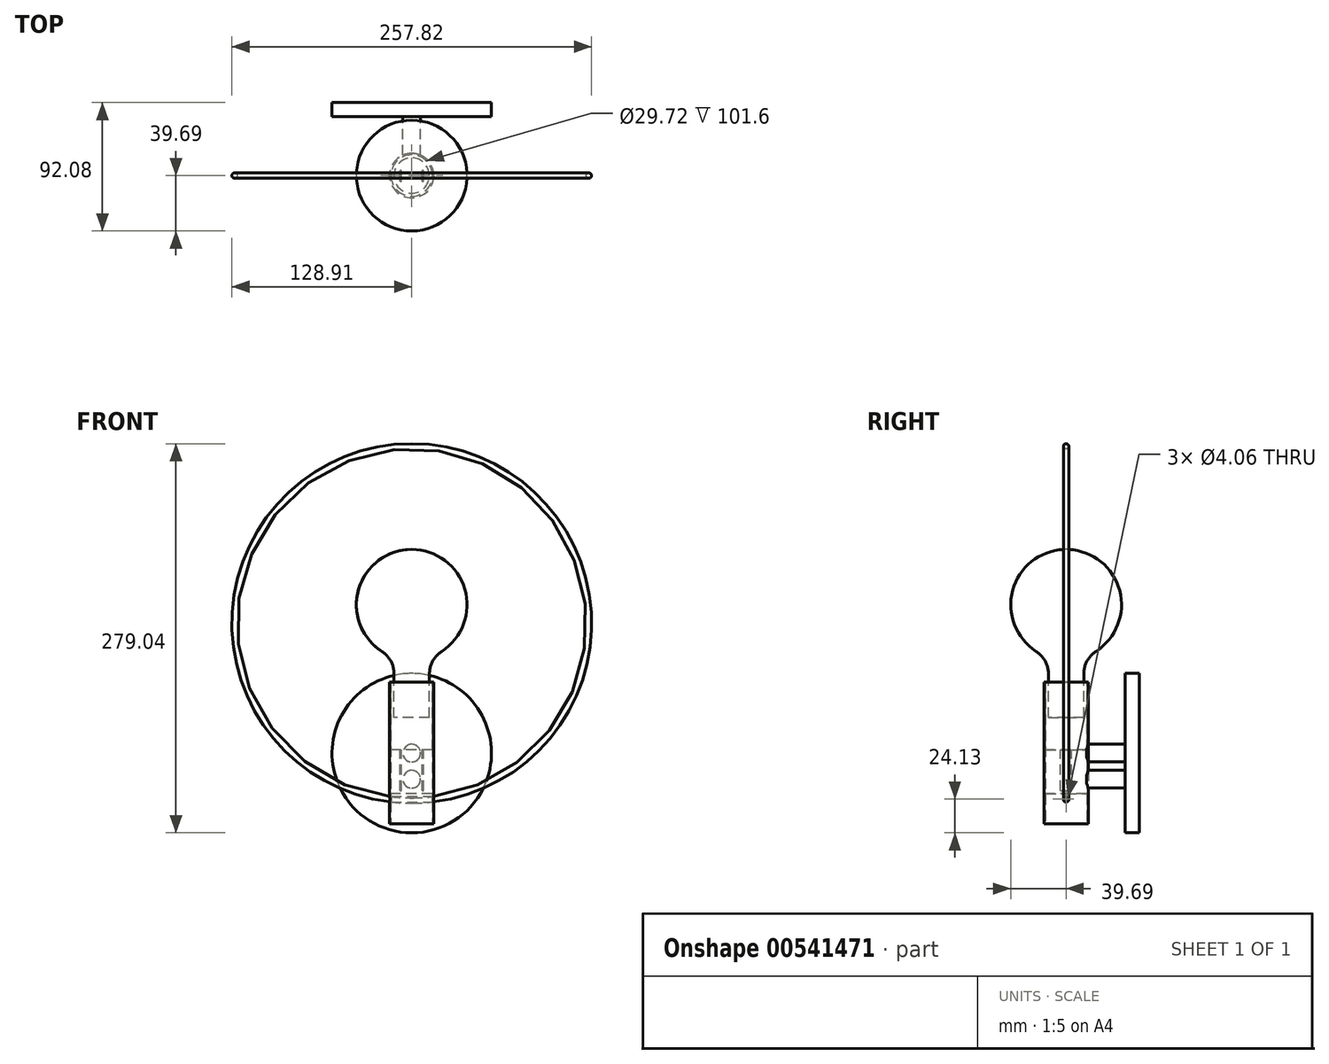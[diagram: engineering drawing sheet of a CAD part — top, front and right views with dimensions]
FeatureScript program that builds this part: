
annotation { "Feature Type Name" : "Feature", "Feature Type Description" : "" }
export const myFeature = defineFeature(function(context is Context, id is Id, definition is map)
    precondition{}
    {
        {
            var Q0;
            Q0=qCreatedBy(makeId("Top.planeOp"),FACE);
            var sketch = newSketch(context, id + "F0", { "sketchPlane" : qUnion([Q0])});
            skCircle(sketch, "E0", {"center": v(0, 0) * mm, "radius": 15.88 * mm});
            skCircle(sketch, "E1", {"center": v(0, 0) * mm, "radius": 14.86 * mm});
            skSolve(sketch);
        }
        {
            var Q0;
            Q0=makeQuery(id+"F0.imprint","IMPRINT",FACE,{"disambiguationData":[TD([[makeQuery(id+"F0.imprint","IMPRINT",EDGE,{"derivedFrom":sQuery(id+"F0.wireOp",EDGE,"E1")}),-1.0]])]});
            extrude(context, id + "F1", {"entities" : qUnion([Q0]), "depth" : 101.6 * mm, "offsetDistance" : 25.4 * mm});
        }
        {
            var Q0;
            Q0=makeQuery(id+"F0.imprint","IMPRINT",FACE,{"disambiguationData":[TD([[makeQuery(id+"F0.imprint","IMPRINT",EDGE,{"derivedFrom":sQuery(id+"F0.wireOp",EDGE,"E1")}),1.0]])]});
            var Q1;
            Q1=sQuery(id+"F0.wireOp",EDGE,"E1");
            extrude(context, id + "F2", {"entities" : qUnion([Q0]), "surfaceEntities" : qUnion([Q1]), "depth" : 21.59 * mm, "offsetDistance" : 25.4 * mm});
        }
        {
            var Q0;
            Q0=qCreatedBy(makeId("Front.planeOp"),FACE);
            var sketch = newSketch(context, id + "F3", { "sketchPlane" : qUnion([Q0])});
            skArc(sketch, "E2", {"start": v(21.45, 123.77) * mm, "mid": v(0, 196.85) * mm, "end": v(-21.45, 123.77) * mm});
            skLineSegment(sketch, "E3.top", {"start": v(-12.7, 76.2) * mm, "end": v(12.7, 76.2) * mm});
            skLineSegment(sketch, "E3.left", {"start": v(-12.7, 107.75) * mm, "end": v(-12.7, 76.2) * mm});
            skLineSegment(sketch, "E3.right", {"start": v(12.7, 107.75) * mm, "end": v(12.7, 76.2) * mm});
            skPoint(sketch, "E4.visualSharp", {"position": v(-12.7, 119.56) * mm});
            skArc(sketch, "E4.filletArc", {"start": v(-12.7, 107.75) * mm, "mid": v(-15.03, 116.88) * mm, "end": v(-21.45, 123.77) * mm});
            skPoint(sketch, "E5.visualSharp", {"position": v(12.7, 119.56) * mm});
            skArc(sketch, "E5.filletArc", {"start": v(21.45, 123.77) * mm, "mid": v(15.03, 116.88) * mm, "end": v(12.7, 107.75) * mm});
            skLineSegment(sketch, "E6", {"start": v(0, 196.85) * mm, "end": v(0, 76.2) * mm});
            skSolve(sketch);
        }
        {
            var Q0;
            {var subQ0=sQuery(id+"F3.wireOp",EDGE,"E3.left");Q0=makeQuery(id+"F3.imprint","IMPRINT",FACE,{"disambiguationData":[TD([[makeQuery(id+"F3.imprint","IMPRINT",EDGE,{"derivedFrom":subQ0}),1.0]])]});}
            var Q1;
            Q1=sQuery(id+"F3.wireOp",EDGE,"E6");
            revolve(context, id + "F4", {"entities" : qUnion([Q0]), "axis" : qUnion([Q1]), "revolveType" : RevolveType.FULL});
        }
        {
            var Q0;
            Q0=qCreatedBy(makeId("Right.planeOp"),FACE);
            var sketch = newSketch(context, id + "F5", { "sketchPlane" : qUnion([Q0])});
            skCircle(sketch, "E7", {"center": v(0, 17.78) * mm, "radius": 2.03 * mm});
            skSolve(sketch);
        }
        {
            var Q0;
            Q0=qSketchRegion(id+"F5",true);
            extrude(context, id + "F6", {"entities" : qUnion([Q0]), "operationType" : NewBodyOperationType.REMOVE, "endBound" : BoundingType.THROUGH_ALL, "oppositeDirection" : true, "depth" : 25.4 * mm, "offsetDistance" : 25.4 * mm, "hasSecondDirection" : true, "secondDirectionBound" : BoundingType.THROUGH_ALL, "secondDirectionOppositeDirection" : false, "secondDirectionDepth" : 25.4 * mm});
        }
        {
            var Q0;
            Q0=qCreatedBy(makeId("Front.planeOp"),FACE);
            var sketch = newSketch(context, id + "F7", { "sketchPlane" : qUnion([Q0])});
            skCircle(sketch, "E8", {"center": v(0, 143.78) * mm, "radius": 127 * mm});
            skFitSpline(sketch, "E9.0", {"points": [v(-15.88, 19.81) * mm, v(-15.88, 19.81) * mm, v(-15.86, 19.7) * mm, v(-15.8, 19.25) * mm, v(-15.77, 18.7) * mm, v(-15.75, 18.18) * mm, v(-15.74, 17.78) * mm, v(-15.75, 17.38) * mm, v(-15.76, 17) * mm, v(-15.78, 16.64) * mm, v(-15.82, 16.23) * mm, v(-15.86, 15.85) * mm, v(-15.88, 15.75) * mm, v(-15.87, 15.75) * mm], "construction": true});
            skLineSegment(sketch, "E10", {"start": v(-15.88, 19.81) * mm, "end": v(-15.87, 15.75) * mm, "construction": true});
            skPoint(sketch, "E11", {"position": v(-15.87, 17.78) * mm});
            skSolve(sketch);
        }
        {
            var Q0;
            Q0=qCreatedBy(makeId("Right.planeOp"),FACE);
            var sketch = newSketch(context, id + "F8", { "sketchPlane" : qUnion([Q0])});
            skCircle(sketch, "E12", {"center": v(0, 16.78) * mm, "radius": 1.9 * mm});
            skSolve(sketch);
        }
        {
            var Q0;
            Q0=qSketchRegion(id+"F8",true);
            var Q1;
            Q1=qConstructionFilter(qBodyType(qCreatedBy(id+"F7",EDGE),BodyType.WIRE),ConstructionObject.NO);
            sweep(context, id + "F9", {"profiles" : qUnion([Q0]), "path" : qUnion([Q1])});
        }
        {
            var Q0;
            Q0=qCreatedBy(makeId("Right.planeOp"),FACE);
            var sketch = newSketch(context, id + "F10", { "sketchPlane" : qUnion([Q0])});
            skArc(sketch, "E13", {"start": v(21.45, 123.77) * mm, "mid": v(0, 196.85) * mm, "end": v(-21.45, 123.77) * mm});
            skLineSegment(sketch, "E14", {"start": v(39.69, 157.16) * mm, "end": v(39.69, 209.78) * mm});
            skSolve(sketch);
        }
        {
            var Q0;
            Q0=qCreatedBy(makeId("Front.planeOp"),FACE);
            var Q1;
            Q1=sQuery(id+"F10.wireOp",VERTEX,"E14.end");
            cPlane(context, id + "F11", {"entities" : qUnion([Q0, Q1]), "cplaneType" : CPlaneType.PLANE_POINT, "offset" : 25.4 * mm, "width" : 152.4 * mm, "height" : 152.4 * mm});
        }
        {
            var Q0;
            Q0=qCreatedBy(id+"F11.planeOp",FACE);
            cPlane(context, id + "F12", {"entities" : qUnion([Q0]), "cplaneType" : CPlaneType.OFFSET, "offset" : 2.54 * mm, "oppositeDirection" : true, "width" : 152.4 * mm, "height" : 152.4 * mm});
        }
        {
            var Q0;
            Q0=qCreatedBy(id+"F12.planeOp",FACE);
            var sketch = newSketch(context, id + "F13", { "sketchPlane" : qUnion([Q0])});
            skCircle(sketch, "E15", {"center": v(0, 50.8) * mm, "radius": 57.15 * mm});
            skLineSegment(sketch, "E16.0", {"start": v(-15.88, 101.6) * mm, "end": v(15.88, 101.6) * mm, "construction": true});
            skLineSegment(sketch, "E17.0", {"start": v(-15.88, 0) * mm, "end": v(15.88, 0) * mm, "construction": true});
            skLineSegment(sketch, "E18", {"start": v(0, 101.6) * mm, "end": v(0, 0) * mm, "construction": true});
            skCircle(sketch, "E19", {"center": v(0, 50.8) * mm, "radius": 6.35 * mm});
            skCircle(sketch, "E20", {"center": v(0, 32.06) * mm, "radius": 6.35 * mm});
            skSolve(sketch);
        }
        {
            var Q0;
            Q0=makeQuery(id+"F13.imprint","IMPRINT",FACE,{"disambiguationData":[TD([[makeQuery(id+"F13.imprint","IMPRINT",EDGE,{"derivedFrom":sQuery(id+"F13.wireOp",EDGE,"E19")}),1.0]])]});
            var Q1;
            Q1=makeQuery(id+"F13.imprint","IMPRINT",FACE,{"disambiguationData":[TD([[makeQuery(id+"F13.imprint","IMPRINT",EDGE,{"derivedFrom":sQuery(id+"F13.wireOp",EDGE,"E20")}),1.0]])]});
            var Q2;
            Q2=makeQuery(id+"F1.opExtrude","SWEPT_FACE",FACE,{"disambiguationData":[OSD([sQuery(id+"F0.wireOp",EDGE,"E0")])]});
            extrude(context, id + "F14", {"entities" : qUnion([Q0, Q1]), "endBound" : BoundingType.UP_TO_SURFACE, "depth" : 25.4 * mm, "endBoundEntityFace" : qUnion([Q2]), "offsetDistance" : 25.4 * mm});
        }
        {
            var Q0;
            Q0=makeQuery(id+"F13.imprint","IMPRINT",FACE,{"disambiguationData":[TD([[makeQuery(id+"F13.imprint","IMPRINT",EDGE,{"derivedFrom":sQuery(id+"F13.wireOp",EDGE,"E15")}),1.0]])]});
            var Q1;
            Q1=makeQuery(id+"F13.imprint","IMPRINT",FACE,{"disambiguationData":[TD([[makeQuery(id+"F13.imprint","IMPRINT",EDGE,{"derivedFrom":sQuery(id+"F13.wireOp",EDGE,"E20")}),1.0]])]});
            var Q2;
            Q2=makeQuery(id+"F13.imprint","IMPRINT",FACE,{"disambiguationData":[TD([[makeQuery(id+"F13.imprint","IMPRINT",EDGE,{"derivedFrom":sQuery(id+"F13.wireOp",EDGE,"E19")}),1.0]])]});
            extrude(context, id + "F15", {"entities" : qUnion([Q0, Q1, Q2]), "oppositeDirection" : true, "depth" : 10.16 * mm, "offsetDistance" : 25.4 * mm});
        }
        {
            var Q0;
            Q0=makeQuery(id+"F1.opExtrude","CAP_FACE",FACE,{"disambiguationData":[OSD([sQuery(id+"F0.wireOp",EDGE,"E0"),sQuery(id+"F0.wireOp",EDGE,"E1")])],"isStart":false});
            var sketch = newSketch(context, id + "F16", { "sketchPlane" : qUnion([Q0])});
            skCircle(sketch, "E21.0", {"center": v(0, 0) * mm, "radius": 14.86 * mm});
            skSolve(sketch);
        }
        {
            var Q0;
            Q0 = qSketchRegion(id + "F16", true);
            extrude(context, id + "F17", {"entities" : qUnion([Q0]), "oppositeDirection" : true, "depth" : 48.58 * mm, "offsetDistance" : 25.4 * mm});
        }
        {
            var Q0;
            Q0=makeQuery(id+"F17.opExtrude","CAP_FACE",FACE,{"disambiguationData":[OSD([sQuery(id+"F16.wireOp",EDGE,"E21.0")])],"isStart":false});
            var sketch = newSketch(context, id + "F18", { "sketchPlane" : qUnion([Q0])});
            skLineSegment(sketch, "E22.bottom", {"start": v(7.43, 3.97) * mm, "end": v(8.45, 3.97) * mm});
            skLineSegment(sketch, "E22.top", {"start": v(7.43, -3.97) * mm, "end": v(8.45, -3.97) * mm});
            skLineSegment(sketch, "E22.left", {"start": v(7.43, 3.97) * mm, "end": v(7.43, -3.97) * mm});
            skLineSegment(sketch, "E22.right", {"start": v(8.45, 3.97) * mm, "end": v(8.45, -3.97) * mm});
            skLineSegment(sketch, "E23.bottom", {"start": v(-8.45, 3.97) * mm, "end": v(-7.43, 3.97) * mm});
            skLineSegment(sketch, "E23.top", {"start": v(-8.45, -3.97) * mm, "end": v(-7.43, -3.97) * mm});
            skLineSegment(sketch, "E23.left", {"start": v(-8.45, 3.97) * mm, "end": v(-8.45, -3.97) * mm});
            skLineSegment(sketch, "E23.right", {"start": v(-7.43, 3.97) * mm, "end": v(-7.43, -3.97) * mm});
            skLineSegment(sketch, "E24", {"start": v(-7.43, 0) * mm, "end": v(7.43, 0) * mm});
            skPoint(sketch, "E25", {"position": v(0, 0) * mm});
            skSolve(sketch);
        }
        {
            var Q0;
            Q0 = qSketchRegion(id + "F18", true);
            extrude(context, id + "F19", {"entities" : qUnion([Q0]), "operationType" : NewBodyOperationType.ADD, "depth" : 29.2 * mm, "offsetDistance" : 25.4 * mm});
        }
    });
